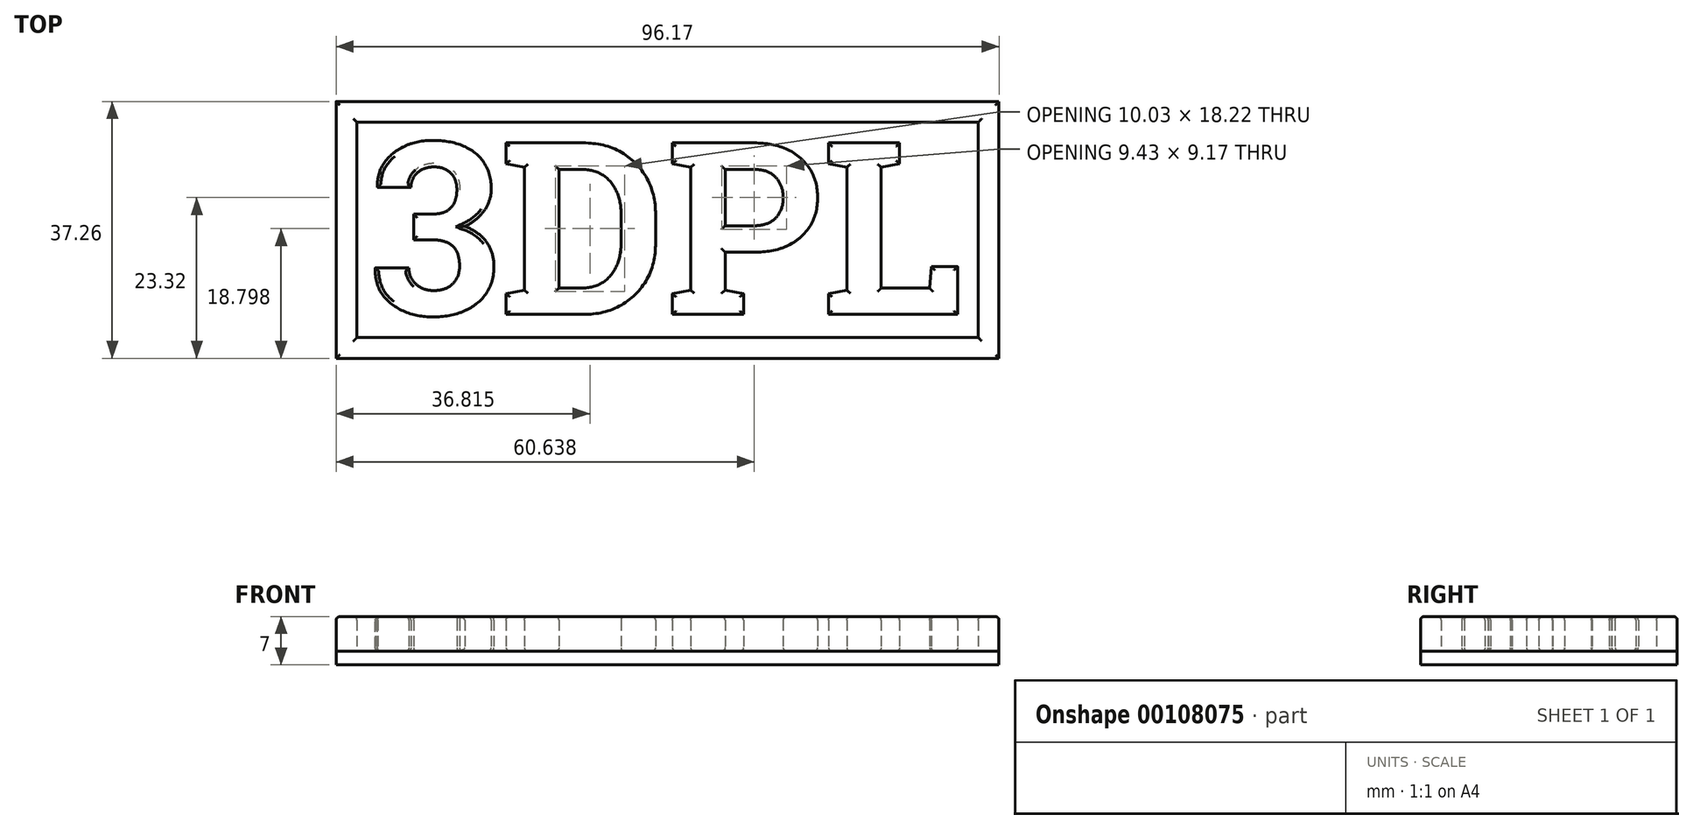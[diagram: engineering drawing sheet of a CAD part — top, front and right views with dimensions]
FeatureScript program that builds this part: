
annotation { "Feature Type Name" : "Feature", "Feature Type Description" : "" }
export const myFeature = defineFeature(function(context is Context, id is Id, definition is map)
    precondition{}
    {
        {
            var Q0;
            Q0=qCreatedBy(makeId("Top.planeOp"),FACE);
            var sketch = newSketch(context, id + "F0", { "sketchPlane" : qUnion([Q0])});
            skText(sketch, "E0", { "text": "3DPL", "fontName": "RobotoSlab-Bold.ttf"});
            const initialGuessF0  = {"E0": [-0.03451, -0.01253, 1, 0, 0.02521]};
            skSetInitialGuess(sketch, initialGuessF0);
            skSolve(sketch);
        }
        {
            var Q0;
            Q0=makeQuery(id+"F0.imprint","IMPRINT",FACE,{"disambiguationData":[TD([[makeQuery(id+"F0.imprint","IMPRINT",EDGE,{"derivedFrom":sQuery(id+"F0.wireOp",EDGE,"E0.sketch_text.stroke-0")}),-1.0]])]});
            var Q1;
            Q1=makeQuery(id+"F0.imprint","IMPRINT",FACE,{"disambiguationData":[TD([[makeQuery(id+"F0.imprint","IMPRINT",EDGE,{"derivedFrom":sQuery(id+"F0.wireOp",EDGE,"E0.sketch_text.stroke-31")}),-1.0]])]});
            var Q2;
            Q2=makeQuery(id+"F0.imprint","IMPRINT",FACE,{"disambiguationData":[TD([[makeQuery(id+"F0.imprint","IMPRINT",EDGE,{"derivedFrom":sQuery(id+"F0.wireOp",EDGE,"E0.sketch_text.stroke-52")}),-1.0]])]});
            var Q3;
            Q3=makeQuery(id+"F0.imprint","IMPRINT",FACE,{"disambiguationData":[TD([[makeQuery(id+"F0.imprint","IMPRINT",EDGE,{"derivedFrom":sQuery(id+"F0.wireOp",EDGE,"E0.sketch_text.stroke-75")}),-1.0]])]});
            extrude(context, id + "F1", {"entities" : qUnion([Q0, Q1, Q2, Q3]), "depth" : 5 * mm});
        }
        {
            var Q0;
            Q0=makeQuery(id+"F1.opExtrude","CAP_FACE",FACE,{"disambiguationData":[OSD([sQuery(id+"F0.wireOp",EDGE,"E0.sketch_text.stroke-0"),sQuery(id+"F0.wireOp",EDGE,"E0.sketch_text.stroke-1"),sQuery(id+"F0.wireOp",EDGE,"E0.sketch_text.stroke-2"),sQuery(id+"F0.wireOp",EDGE,"E0.sketch_text.stroke-3"),sQuery(id+"F0.wireOp",EDGE,"E0.sketch_text.stroke-4"),sQuery(id+"F0.wireOp",EDGE,"E0.sketch_text.stroke-5"),sQuery(id+"F0.wireOp",EDGE,"E0.sketch_text.stroke-6"),sQuery(id+"F0.wireOp",EDGE,"E0.sketch_text.stroke-7"),sQuery(id+"F0.wireOp",EDGE,"E0.sketch_text.stroke-8"),sQuery(id+"F0.wireOp",EDGE,"E0.sketch_text.stroke-9"),sQuery(id+"F0.wireOp",EDGE,"E0.sketch_text.stroke-10"),sQuery(id+"F0.wireOp",EDGE,"E0.sketch_text.stroke-11"),sQuery(id+"F0.wireOp",EDGE,"E0.sketch_text.stroke-12"),sQuery(id+"F0.wireOp",EDGE,"E0.sketch_text.stroke-13"),sQuery(id+"F0.wireOp",EDGE,"E0.sketch_text.stroke-14"),sQuery(id+"F0.wireOp",EDGE,"E0.sketch_text.stroke-15"),sQuery(id+"F0.wireOp",EDGE,"E0.sketch_text.stroke-16"),sQuery(id+"F0.wireOp",EDGE,"E0.sketch_text.stroke-17"),sQuery(id+"F0.wireOp",EDGE,"E0.sketch_text.stroke-18"),sQuery(id+"F0.wireOp",EDGE,"E0.sketch_text.stroke-19"),sQuery(id+"F0.wireOp",EDGE,"E0.sketch_text.stroke-20"),sQuery(id+"F0.wireOp",EDGE,"E0.sketch_text.stroke-21"),sQuery(id+"F0.wireOp",EDGE,"E0.sketch_text.stroke-22"),sQuery(id+"F0.wireOp",EDGE,"E0.sketch_text.stroke-23"),sQuery(id+"F0.wireOp",EDGE,"E0.sketch_text.stroke-24"),sQuery(id+"F0.wireOp",EDGE,"E0.sketch_text.stroke-25"),sQuery(id+"F0.wireOp",EDGE,"E0.sketch_text.stroke-26"),sQuery(id+"F0.wireOp",EDGE,"E0.sketch_text.stroke-27"),sQuery(id+"F0.wireOp",EDGE,"E0.sketch_text.stroke-28"),sQuery(id+"F0.wireOp",EDGE,"E0.sketch_text.stroke-29"),sQuery(id+"F0.wireOp",EDGE,"E0.sketch_text.stroke-30")])],"isStart":false});
            var Q1;
            Q1=makeQuery(id+"F1.opExtrude","CAP_FACE",FACE,{"disambiguationData":[OSD([sQuery(id+"F0.wireOp",EDGE,"E0.sketch_text.stroke-31"),sQuery(id+"F0.wireOp",EDGE,"E0.sketch_text.stroke-32"),sQuery(id+"F0.wireOp",EDGE,"E0.sketch_text.stroke-33"),sQuery(id+"F0.wireOp",EDGE,"E0.sketch_text.stroke-34"),sQuery(id+"F0.wireOp",EDGE,"E0.sketch_text.stroke-35"),sQuery(id+"F0.wireOp",EDGE,"E0.sketch_text.stroke-36"),sQuery(id+"F0.wireOp",EDGE,"E0.sketch_text.stroke-37"),sQuery(id+"F0.wireOp",EDGE,"E0.sketch_text.stroke-38"),sQuery(id+"F0.wireOp",EDGE,"E0.sketch_text.stroke-39"),sQuery(id+"F0.wireOp",EDGE,"E0.sketch_text.stroke-40"),sQuery(id+"F0.wireOp",EDGE,"E0.sketch_text.stroke-41"),sQuery(id+"F0.wireOp",EDGE,"E0.sketch_text.stroke-42"),sQuery(id+"F0.wireOp",EDGE,"E0.sketch_text.stroke-43"),sQuery(id+"F0.wireOp",EDGE,"E0.sketch_text.stroke-44"),sQuery(id+"F0.wireOp",EDGE,"E0.sketch_text.stroke-45"),sQuery(id+"F0.wireOp",EDGE,"E0.sketch_text.stroke-46"),sQuery(id+"F0.wireOp",EDGE,"E0.sketch_text.stroke-47"),sQuery(id+"F0.wireOp",EDGE,"E0.sketch_text.stroke-48"),sQuery(id+"F0.wireOp",EDGE,"E0.sketch_text.stroke-49"),sQuery(id+"F0.wireOp",EDGE,"E0.sketch_text.stroke-50"),sQuery(id+"F0.wireOp",EDGE,"E0.sketch_text.stroke-51")])],"isStart":false});
            var Q2;
            Q2=makeQuery(id+"F1.opExtrude","CAP_FACE",FACE,{"disambiguationData":[OSD([sQuery(id+"F0.wireOp",EDGE,"E0.sketch_text.stroke-52"),sQuery(id+"F0.wireOp",EDGE,"E0.sketch_text.stroke-53"),sQuery(id+"F0.wireOp",EDGE,"E0.sketch_text.stroke-54"),sQuery(id+"F0.wireOp",EDGE,"E0.sketch_text.stroke-55"),sQuery(id+"F0.wireOp",EDGE,"E0.sketch_text.stroke-56"),sQuery(id+"F0.wireOp",EDGE,"E0.sketch_text.stroke-57"),sQuery(id+"F0.wireOp",EDGE,"E0.sketch_text.stroke-58"),sQuery(id+"F0.wireOp",EDGE,"E0.sketch_text.stroke-59"),sQuery(id+"F0.wireOp",EDGE,"E0.sketch_text.stroke-60"),sQuery(id+"F0.wireOp",EDGE,"E0.sketch_text.stroke-61"),sQuery(id+"F0.wireOp",EDGE,"E0.sketch_text.stroke-62"),sQuery(id+"F0.wireOp",EDGE,"E0.sketch_text.stroke-63"),sQuery(id+"F0.wireOp",EDGE,"E0.sketch_text.stroke-64"),sQuery(id+"F0.wireOp",EDGE,"E0.sketch_text.stroke-65"),sQuery(id+"F0.wireOp",EDGE,"E0.sketch_text.stroke-66"),sQuery(id+"F0.wireOp",EDGE,"E0.sketch_text.stroke-67"),sQuery(id+"F0.wireOp",EDGE,"E0.sketch_text.stroke-68"),sQuery(id+"F0.wireOp",EDGE,"E0.sketch_text.stroke-69"),sQuery(id+"F0.wireOp",EDGE,"E0.sketch_text.stroke-70"),sQuery(id+"F0.wireOp",EDGE,"E0.sketch_text.stroke-71"),sQuery(id+"F0.wireOp",EDGE,"E0.sketch_text.stroke-72"),sQuery(id+"F0.wireOp",EDGE,"E0.sketch_text.stroke-73"),sQuery(id+"F0.wireOp",EDGE,"E0.sketch_text.stroke-74")])],"isStart":false});
            var Q3;
            Q3=makeQuery(id+"F1.opExtrude","CAP_FACE",FACE,{"disambiguationData":[OSD([sQuery(id+"F0.wireOp",EDGE,"E0.sketch_text.stroke-75"),sQuery(id+"F0.wireOp",EDGE,"E0.sketch_text.stroke-76"),sQuery(id+"F0.wireOp",EDGE,"E0.sketch_text.stroke-77"),sQuery(id+"F0.wireOp",EDGE,"E0.sketch_text.stroke-78"),sQuery(id+"F0.wireOp",EDGE,"E0.sketch_text.stroke-79"),sQuery(id+"F0.wireOp",EDGE,"E0.sketch_text.stroke-80"),sQuery(id+"F0.wireOp",EDGE,"E0.sketch_text.stroke-81"),sQuery(id+"F0.wireOp",EDGE,"E0.sketch_text.stroke-82"),sQuery(id+"F0.wireOp",EDGE,"E0.sketch_text.stroke-83"),sQuery(id+"F0.wireOp",EDGE,"E0.sketch_text.stroke-84"),sQuery(id+"F0.wireOp",EDGE,"E0.sketch_text.stroke-85"),sQuery(id+"F0.wireOp",EDGE,"E0.sketch_text.stroke-86"),sQuery(id+"F0.wireOp",EDGE,"E0.sketch_text.stroke-87"),sQuery(id+"F0.wireOp",EDGE,"E0.sketch_text.stroke-88"),sQuery(id+"F0.wireOp",EDGE,"E0.sketch_text.stroke-89"),sQuery(id+"F0.wireOp",EDGE,"E0.sketch_text.stroke-90")])],"isStart":false});
            var Q4;
            Q4=makeQuery(id+"F1.opExtrude","CAP_FACE",FACE,{"disambiguationData":[OSD([sQuery(id+"F0.wireOp",EDGE,"E0.sketch_text.stroke-0"),sQuery(id+"F0.wireOp",EDGE,"E0.sketch_text.stroke-1"),sQuery(id+"F0.wireOp",EDGE,"E0.sketch_text.stroke-2"),sQuery(id+"F0.wireOp",EDGE,"E0.sketch_text.stroke-3"),sQuery(id+"F0.wireOp",EDGE,"E0.sketch_text.stroke-4"),sQuery(id+"F0.wireOp",EDGE,"E0.sketch_text.stroke-5"),sQuery(id+"F0.wireOp",EDGE,"E0.sketch_text.stroke-6"),sQuery(id+"F0.wireOp",EDGE,"E0.sketch_text.stroke-7"),sQuery(id+"F0.wireOp",EDGE,"E0.sketch_text.stroke-8"),sQuery(id+"F0.wireOp",EDGE,"E0.sketch_text.stroke-9"),sQuery(id+"F0.wireOp",EDGE,"E0.sketch_text.stroke-10"),sQuery(id+"F0.wireOp",EDGE,"E0.sketch_text.stroke-11"),sQuery(id+"F0.wireOp",EDGE,"E0.sketch_text.stroke-12"),sQuery(id+"F0.wireOp",EDGE,"E0.sketch_text.stroke-13"),sQuery(id+"F0.wireOp",EDGE,"E0.sketch_text.stroke-14"),sQuery(id+"F0.wireOp",EDGE,"E0.sketch_text.stroke-15"),sQuery(id+"F0.wireOp",EDGE,"E0.sketch_text.stroke-16"),sQuery(id+"F0.wireOp",EDGE,"E0.sketch_text.stroke-17"),sQuery(id+"F0.wireOp",EDGE,"E0.sketch_text.stroke-18"),sQuery(id+"F0.wireOp",EDGE,"E0.sketch_text.stroke-19"),sQuery(id+"F0.wireOp",EDGE,"E0.sketch_text.stroke-20"),sQuery(id+"F0.wireOp",EDGE,"E0.sketch_text.stroke-21"),sQuery(id+"F0.wireOp",EDGE,"E0.sketch_text.stroke-22"),sQuery(id+"F0.wireOp",EDGE,"E0.sketch_text.stroke-23"),sQuery(id+"F0.wireOp",EDGE,"E0.sketch_text.stroke-24"),sQuery(id+"F0.wireOp",EDGE,"E0.sketch_text.stroke-25"),sQuery(id+"F0.wireOp",EDGE,"E0.sketch_text.stroke-26"),sQuery(id+"F0.wireOp",EDGE,"E0.sketch_text.stroke-27"),sQuery(id+"F0.wireOp",EDGE,"E0.sketch_text.stroke-28"),sQuery(id+"F0.wireOp",EDGE,"E0.sketch_text.stroke-29"),sQuery(id+"F0.wireOp",EDGE,"E0.sketch_text.stroke-30")])],"isStart":true});
            var Q5;
            Q5=makeQuery(id+"F1.opExtrude","CAP_FACE",FACE,{"disambiguationData":[OSD([sQuery(id+"F0.wireOp",EDGE,"E0.sketch_text.stroke-31"),sQuery(id+"F0.wireOp",EDGE,"E0.sketch_text.stroke-32"),sQuery(id+"F0.wireOp",EDGE,"E0.sketch_text.stroke-33"),sQuery(id+"F0.wireOp",EDGE,"E0.sketch_text.stroke-34"),sQuery(id+"F0.wireOp",EDGE,"E0.sketch_text.stroke-35"),sQuery(id+"F0.wireOp",EDGE,"E0.sketch_text.stroke-36"),sQuery(id+"F0.wireOp",EDGE,"E0.sketch_text.stroke-37"),sQuery(id+"F0.wireOp",EDGE,"E0.sketch_text.stroke-38"),sQuery(id+"F0.wireOp",EDGE,"E0.sketch_text.stroke-39"),sQuery(id+"F0.wireOp",EDGE,"E0.sketch_text.stroke-40"),sQuery(id+"F0.wireOp",EDGE,"E0.sketch_text.stroke-41"),sQuery(id+"F0.wireOp",EDGE,"E0.sketch_text.stroke-42"),sQuery(id+"F0.wireOp",EDGE,"E0.sketch_text.stroke-43"),sQuery(id+"F0.wireOp",EDGE,"E0.sketch_text.stroke-44"),sQuery(id+"F0.wireOp",EDGE,"E0.sketch_text.stroke-45"),sQuery(id+"F0.wireOp",EDGE,"E0.sketch_text.stroke-46"),sQuery(id+"F0.wireOp",EDGE,"E0.sketch_text.stroke-47"),sQuery(id+"F0.wireOp",EDGE,"E0.sketch_text.stroke-48"),sQuery(id+"F0.wireOp",EDGE,"E0.sketch_text.stroke-49"),sQuery(id+"F0.wireOp",EDGE,"E0.sketch_text.stroke-50"),sQuery(id+"F0.wireOp",EDGE,"E0.sketch_text.stroke-51")])],"isStart":true});
            var Q6;
            Q6=makeQuery(id+"F1.opExtrude","CAP_FACE",FACE,{"disambiguationData":[OSD([sQuery(id+"F0.wireOp",EDGE,"E0.sketch_text.stroke-52"),sQuery(id+"F0.wireOp",EDGE,"E0.sketch_text.stroke-53"),sQuery(id+"F0.wireOp",EDGE,"E0.sketch_text.stroke-54"),sQuery(id+"F0.wireOp",EDGE,"E0.sketch_text.stroke-55"),sQuery(id+"F0.wireOp",EDGE,"E0.sketch_text.stroke-56"),sQuery(id+"F0.wireOp",EDGE,"E0.sketch_text.stroke-57"),sQuery(id+"F0.wireOp",EDGE,"E0.sketch_text.stroke-58"),sQuery(id+"F0.wireOp",EDGE,"E0.sketch_text.stroke-59"),sQuery(id+"F0.wireOp",EDGE,"E0.sketch_text.stroke-60"),sQuery(id+"F0.wireOp",EDGE,"E0.sketch_text.stroke-61"),sQuery(id+"F0.wireOp",EDGE,"E0.sketch_text.stroke-62"),sQuery(id+"F0.wireOp",EDGE,"E0.sketch_text.stroke-63"),sQuery(id+"F0.wireOp",EDGE,"E0.sketch_text.stroke-64"),sQuery(id+"F0.wireOp",EDGE,"E0.sketch_text.stroke-65"),sQuery(id+"F0.wireOp",EDGE,"E0.sketch_text.stroke-66"),sQuery(id+"F0.wireOp",EDGE,"E0.sketch_text.stroke-67"),sQuery(id+"F0.wireOp",EDGE,"E0.sketch_text.stroke-68"),sQuery(id+"F0.wireOp",EDGE,"E0.sketch_text.stroke-69"),sQuery(id+"F0.wireOp",EDGE,"E0.sketch_text.stroke-70"),sQuery(id+"F0.wireOp",EDGE,"E0.sketch_text.stroke-71"),sQuery(id+"F0.wireOp",EDGE,"E0.sketch_text.stroke-72"),sQuery(id+"F0.wireOp",EDGE,"E0.sketch_text.stroke-73"),sQuery(id+"F0.wireOp",EDGE,"E0.sketch_text.stroke-74")])],"isStart":true});
            var Q7;
            Q7=makeQuery(id+"F1.opExtrude","CAP_FACE",FACE,{"disambiguationData":[OSD([sQuery(id+"F0.wireOp",EDGE,"E0.sketch_text.stroke-75"),sQuery(id+"F0.wireOp",EDGE,"E0.sketch_text.stroke-76"),sQuery(id+"F0.wireOp",EDGE,"E0.sketch_text.stroke-77"),sQuery(id+"F0.wireOp",EDGE,"E0.sketch_text.stroke-78"),sQuery(id+"F0.wireOp",EDGE,"E0.sketch_text.stroke-79"),sQuery(id+"F0.wireOp",EDGE,"E0.sketch_text.stroke-80"),sQuery(id+"F0.wireOp",EDGE,"E0.sketch_text.stroke-81"),sQuery(id+"F0.wireOp",EDGE,"E0.sketch_text.stroke-82"),sQuery(id+"F0.wireOp",EDGE,"E0.sketch_text.stroke-83"),sQuery(id+"F0.wireOp",EDGE,"E0.sketch_text.stroke-84"),sQuery(id+"F0.wireOp",EDGE,"E0.sketch_text.stroke-85"),sQuery(id+"F0.wireOp",EDGE,"E0.sketch_text.stroke-86"),sQuery(id+"F0.wireOp",EDGE,"E0.sketch_text.stroke-87"),sQuery(id+"F0.wireOp",EDGE,"E0.sketch_text.stroke-88"),sQuery(id+"F0.wireOp",EDGE,"E0.sketch_text.stroke-89"),sQuery(id+"F0.wireOp",EDGE,"E0.sketch_text.stroke-90")])],"isStart":true});
            fillet(context, id + "F2", {"entities" : qUnion([Q0, Q1, Q2, Q3, Q4, Q5, Q6, Q7]), "radius" : 0.5 * mm, "tangentPropagation" : true, "allowEdgeOverflow" : false});
        }
        {
            var Q0;
            Q0=qCreatedBy(makeId("Top.planeOp"),FACE);
            var sketch = newSketch(context, id + "F3", { "sketchPlane" : qUnion([Q0])});
            skLineSegment(sketch, "E1.bottom", {"start": v(-39.2, -18.9) * mm, "end": v(56.97, -18.9) * mm});
            skLineSegment(sketch, "E1.top", {"start": v(-39.2, 18.37) * mm, "end": v(56.97, 18.37) * mm});
            skLineSegment(sketch, "E1.left", {"start": v(-39.2, -18.9) * mm, "end": v(-39.2, 18.37) * mm});
            skLineSegment(sketch, "E1.right", {"start": v(56.97, -18.9) * mm, "end": v(56.97, 18.37) * mm});
            skPoint(sketch, "E1.middle", {"position": v(8.88, -0.26) * mm});
            skLineSegment(sketch, "E2.bottom", {"start": v(-36.2, -15.9) * mm, "end": v(53.97, -15.9) * mm});
            skLineSegment(sketch, "E2.top", {"start": v(-36.2, 15.37) * mm, "end": v(53.97, 15.37) * mm});
            skLineSegment(sketch, "E2.left", {"start": v(-36.2, -15.9) * mm, "end": v(-36.2, 15.37) * mm});
            skLineSegment(sketch, "E2.right", {"start": v(53.97, -15.9) * mm, "end": v(53.97, 15.37) * mm});
            skSolve(sketch);
        }
        {
            var Q0;
            Q0=makeQuery(id+"F3.imprint","IMPRINT",FACE,{"disambiguationData":[TD([[makeQuery(id+"F3.imprint","IMPRINT",EDGE,{"derivedFrom":sQuery(id+"F3.wireOp",EDGE,"E2.bottom")}),1.0]])]});
            var Q1;
            Q1=makeQuery(id+"F3.imprint","IMPRINT",FACE,{"disambiguationData":[TD([[makeQuery(id+"F3.imprint","IMPRINT",EDGE,{"derivedFrom":sQuery(id+"F3.wireOp",EDGE,"E1.bottom")}),1.0]])]});
            extrude(context, id + "F4", {"entities" : qUnion([Q0, Q1]), "oppositeDirection" : true, "depth" : 2 * mm});
        }
        {
            var Q0;
            Q0=makeQuery(id+"F3.imprint","IMPRINT",FACE,{"disambiguationData":[TD([[makeQuery(id+"F3.imprint","IMPRINT",EDGE,{"derivedFrom":sQuery(id+"F3.wireOp",EDGE,"E1.bottom")}),1.0]])]});
            var Q1;
            Q1=makeQuery(id+"F1.opExtrude","CAP_FACE",FACE,{"disambiguationData":[OSD([sQuery(id+"F0.wireOp",EDGE,"E0.sketch_text.stroke-0"),sQuery(id+"F0.wireOp",EDGE,"E0.sketch_text.stroke-1"),sQuery(id+"F0.wireOp",EDGE,"E0.sketch_text.stroke-2"),sQuery(id+"F0.wireOp",EDGE,"E0.sketch_text.stroke-3"),sQuery(id+"F0.wireOp",EDGE,"E0.sketch_text.stroke-4"),sQuery(id+"F0.wireOp",EDGE,"E0.sketch_text.stroke-5"),sQuery(id+"F0.wireOp",EDGE,"E0.sketch_text.stroke-6"),sQuery(id+"F0.wireOp",EDGE,"E0.sketch_text.stroke-7"),sQuery(id+"F0.wireOp",EDGE,"E0.sketch_text.stroke-8"),sQuery(id+"F0.wireOp",EDGE,"E0.sketch_text.stroke-9"),sQuery(id+"F0.wireOp",EDGE,"E0.sketch_text.stroke-10"),sQuery(id+"F0.wireOp",EDGE,"E0.sketch_text.stroke-11"),sQuery(id+"F0.wireOp",EDGE,"E0.sketch_text.stroke-12"),sQuery(id+"F0.wireOp",EDGE,"E0.sketch_text.stroke-13"),sQuery(id+"F0.wireOp",EDGE,"E0.sketch_text.stroke-14"),sQuery(id+"F0.wireOp",EDGE,"E0.sketch_text.stroke-15"),sQuery(id+"F0.wireOp",EDGE,"E0.sketch_text.stroke-16"),sQuery(id+"F0.wireOp",EDGE,"E0.sketch_text.stroke-17"),sQuery(id+"F0.wireOp",EDGE,"E0.sketch_text.stroke-18"),sQuery(id+"F0.wireOp",EDGE,"E0.sketch_text.stroke-19"),sQuery(id+"F0.wireOp",EDGE,"E0.sketch_text.stroke-20"),sQuery(id+"F0.wireOp",EDGE,"E0.sketch_text.stroke-21"),sQuery(id+"F0.wireOp",EDGE,"E0.sketch_text.stroke-22"),sQuery(id+"F0.wireOp",EDGE,"E0.sketch_text.stroke-23"),sQuery(id+"F0.wireOp",EDGE,"E0.sketch_text.stroke-24"),sQuery(id+"F0.wireOp",EDGE,"E0.sketch_text.stroke-25"),sQuery(id+"F0.wireOp",EDGE,"E0.sketch_text.stroke-26"),sQuery(id+"F0.wireOp",EDGE,"E0.sketch_text.stroke-27"),sQuery(id+"F0.wireOp",EDGE,"E0.sketch_text.stroke-28"),sQuery(id+"F0.wireOp",EDGE,"E0.sketch_text.stroke-29"),sQuery(id+"F0.wireOp",EDGE,"E0.sketch_text.stroke-30")])],"isStart":false});
            extrude(context, id + "F5", {"entities" : qUnion([Q0]), "endBound" : BoundingType.UP_TO_SURFACE, "endBoundEntityFace" : qUnion([Q1]), "depth" : 25 * mm});
        }
        {
            var Q0;
            Q0=makeQuery(id+"F5.opExtrude","CAP_FACE",FACE,{"disambiguationData":[OSD([sQuery(id+"F3.wireOp",EDGE,"E1.bottom"),sQuery(id+"F3.wireOp",EDGE,"E1.top"),sQuery(id+"F3.wireOp",EDGE,"E1.left"),sQuery(id+"F3.wireOp",EDGE,"E1.right"),sQuery(id+"F3.wireOp",EDGE,"E2.bottom"),sQuery(id+"F3.wireOp",EDGE,"E2.top"),sQuery(id+"F3.wireOp",EDGE,"E2.left"),sQuery(id+"F3.wireOp",EDGE,"E2.right")])],"isStart":false});
            fillet(context, id + "F6", {"entities" : qUnion([Q0]), "radius" : 0.5 * mm, "tangentPropagation" : true, "allowEdgeOverflow" : false});
        }
    });
